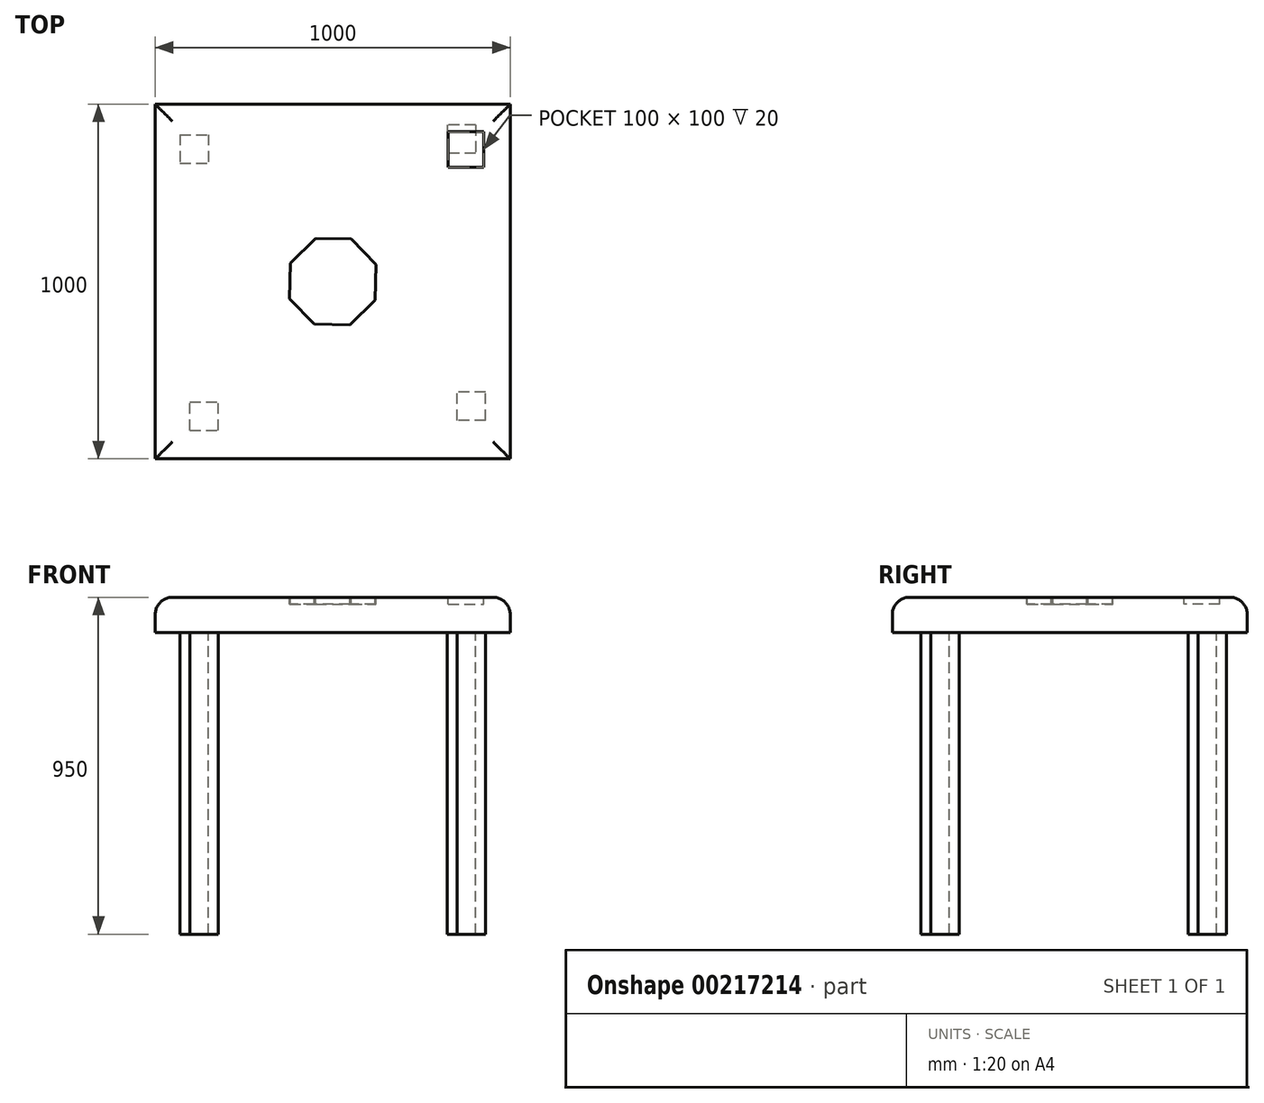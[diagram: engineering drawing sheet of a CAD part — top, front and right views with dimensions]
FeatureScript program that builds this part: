
annotation { "Feature Type Name" : "Feature", "Feature Type Description" : "" }
export const myFeature = defineFeature(function(context is Context, id is Id, definition is map)
    precondition{}
    {
        {
            var Q0;
            Q0=qCreatedBy(makeId("Top.planeOp"),FACE);
            var sketch = newSketch(context, id + "F0", { "sketchPlane" : qUnion([Q0])});
            skLineSegment(sketch, "E0.bottom", {"start": v(-500, 500) * mm, "end": v(500, 500) * mm});
            skLineSegment(sketch, "E0.top", {"start": v(-500, -500) * mm, "end": v(500, -500) * mm});
            skLineSegment(sketch, "E0.left", {"start": v(-500, 500) * mm, "end": v(-500, -500) * mm});
            skLineSegment(sketch, "E0.right", {"start": v(500, 500) * mm, "end": v(500, -500) * mm});
            skSolve(sketch);
        }
        {
            var Q0;
            Q0=makeQuery(id+"F0.imprint","IMPRINT",FACE,{"disambiguationData":[TD([[makeQuery(id+"F0.imprint","IMPRINT",EDGE,{"derivedFrom":sQuery(id+"F0.wireOp",EDGE,"E0.bottom")}),-1.0]])]});
            extrude(context, id + "F1", {"entities" : qUnion([Q0]), "depth" : 100 * mm});
        }
        {
            var Q0;
            Q0=makeQuery(id+"F1.opExtrude","CAP_FACE",FACE,{"disambiguationData":[OSD([sQuery(id+"F0.wireOp",EDGE,"E0.bottom"),sQuery(id+"F0.wireOp",EDGE,"E0.top"),sQuery(id+"F0.wireOp",EDGE,"E0.left"),sQuery(id+"F0.wireOp",EDGE,"E0.right")])],"isStart":false});
            fillet(context, id + "F2", {"entities" : qUnion([Q0]), "radius" : 48.28 * mm, "tangentPropagation" : true, "allowEdgeOverflow" : false});
        }
        {
            var Q0;
            Q0=makeQuery(id+"F1.opExtrude","CAP_FACE",FACE,{"disambiguationData":[OSD([sQuery(id+"F0.wireOp",EDGE,"E0.bottom"),sQuery(id+"F0.wireOp",EDGE,"E0.top"),sQuery(id+"F0.wireOp",EDGE,"E0.left"),sQuery(id+"F0.wireOp",EDGE,"E0.right")])],"isStart":false});
            var sketch = newSketch(context, id + "F3", { "sketchPlane" : qUnion([Q0])});
            skLineSegment(sketch, "E1.0", {"start": v(-119.83, 52.08) * mm, "end": v(-47.9, 121.56) * mm});
            skLineSegment(sketch, "E1.1", {"start": v(-47.9, 121.56) * mm, "end": v(52.08, 119.83) * mm});
            skLineSegment(sketch, "E1.2", {"start": v(52.08, 119.83) * mm, "end": v(121.56, 47.9) * mm});
            skLineSegment(sketch, "E1.3", {"start": v(121.56, 47.9) * mm, "end": v(119.83, -52.08) * mm});
            skLineSegment(sketch, "E1.4", {"start": v(119.83, -52.08) * mm, "end": v(47.9, -121.56) * mm});
            skLineSegment(sketch, "E1.5", {"start": v(47.9, -121.56) * mm, "end": v(-52.08, -119.83) * mm});
            skLineSegment(sketch, "E1.6", {"start": v(-52.08, -119.83) * mm, "end": v(-121.56, -47.9) * mm});
            skLineSegment(sketch, "E1.7", {"start": v(-121.56, -47.9) * mm, "end": v(-119.83, 52.08) * mm});
            skPoint(sketch, "E1.0.midPoint", {"position": v(-83.87, 86.82) * mm});
            skSolve(sketch);
        }
        {
            var Q0;
            Q0=makeQuery(id+"F3.imprint","IMPRINT",FACE,{"disambiguationData":[TD([[makeQuery(id+"F3.imprint","IMPRINT",EDGE,{"derivedFrom":sQuery(id+"F3.wireOp",EDGE,"E1.0")}),-1.0]])]});
            extrude(context, id + "F4", {"entities" : qUnion([Q0]), "operationType" : NewBodyOperationType.REMOVE, "oppositeDirection" : true, "depth" : 20 * mm});
        }
        {
            var Q0;
            Q0=makeQuery(id+"F1.opExtrude","CAP_FACE",FACE,{"disambiguationData":[OSD([sQuery(id+"F0.wireOp",EDGE,"E0.bottom"),sQuery(id+"F0.wireOp",EDGE,"E0.top"),sQuery(id+"F0.wireOp",EDGE,"E0.left"),sQuery(id+"F0.wireOp",EDGE,"E0.right")])],"isStart":false});
            var sketch = newSketch(context, id + "F5", { "sketchPlane" : qUnion([Q0])});
            skLineSegment(sketch, "E2.bottom", {"start": v(325.26, 422.02) * mm, "end": v(425.26, 422.02) * mm});
            skLineSegment(sketch, "E2.top", {"start": v(325.26, 322.02) * mm, "end": v(425.26, 322.02) * mm});
            skLineSegment(sketch, "E2.left", {"start": v(325.26, 422.02) * mm, "end": v(325.26, 322.02) * mm});
            skLineSegment(sketch, "E2.right", {"start": v(425.26, 422.02) * mm, "end": v(425.26, 322.02) * mm});
            skSolve(sketch);
        }
        {
            var Q0;
            Q0=makeQuery(id+"F5.imprint","IMPRINT",FACE,{"disambiguationData":[TD([[makeQuery(id+"F5.imprint","IMPRINT",EDGE,{"derivedFrom":sQuery(id+"F5.wireOp",EDGE,"E2.bottom")}),-1.0]])]});
            extrude(context, id + "F6", {"entities" : qUnion([Q0]), "operationType" : NewBodyOperationType.REMOVE, "oppositeDirection" : true, "depth" : 20 * mm});
        }
        {
            var Q0;
            Q0=makeQuery(id+"F1.opExtrude","CAP_FACE",FACE,{"disambiguationData":[OSD([sQuery(id+"F0.wireOp",EDGE,"E0.bottom"),sQuery(id+"F0.wireOp",EDGE,"E0.top"),sQuery(id+"F0.wireOp",EDGE,"E0.left"),sQuery(id+"F0.wireOp",EDGE,"E0.right")])],"isStart":true});
            var sketch = newSketch(context, id + "F7", { "sketchPlane" : qUnion([Q0])});
            skLineSegment(sketch, "E3.bottom", {"start": v(-402.4, 418.9) * mm, "end": v(-322.4, 418.9) * mm});
            skLineSegment(sketch, "E3.top", {"start": v(-402.4, 338.9) * mm, "end": v(-322.4, 338.9) * mm});
            skLineSegment(sketch, "E3.left", {"start": v(-402.4, 418.9) * mm, "end": v(-402.4, 338.9) * mm});
            skLineSegment(sketch, "E3.right", {"start": v(-322.4, 418.9) * mm, "end": v(-322.4, 338.9) * mm});
            skLineSegment(sketch, "E4.1.0", {"start": v(-350.32, -413.83) * mm, "end": v(-350.32, -333.83) * mm});
            skLineSegment(sketch, "E4.1.1", {"start": v(-430.32, -413.83) * mm, "end": v(-350.32, -413.83) * mm});
            skLineSegment(sketch, "E4.1.2", {"start": v(-430.32, -333.83) * mm, "end": v(-350.32, -333.83) * mm});
            skLineSegment(sketch, "E4.1.3", {"start": v(-430.32, -413.83) * mm, "end": v(-430.32, -333.83) * mm});
            skLineSegment(sketch, "E4.2.0", {"start": v(402.4, -361.75) * mm, "end": v(322.4, -361.75) * mm});
            skLineSegment(sketch, "E4.2.1", {"start": v(402.4, -441.75) * mm, "end": v(402.4, -361.75) * mm});
            skLineSegment(sketch, "E4.2.2", {"start": v(322.4, -441.75) * mm, "end": v(322.4, -361.75) * mm});
            skLineSegment(sketch, "E4.2.3", {"start": v(402.4, -441.75) * mm, "end": v(322.4, -441.75) * mm});
            skLineSegment(sketch, "E4.3.0", {"start": v(350.32, 390.97) * mm, "end": v(350.32, 310.97) * mm});
            skLineSegment(sketch, "E4.3.1", {"start": v(430.32, 390.97) * mm, "end": v(350.32, 390.97) * mm});
            skLineSegment(sketch, "E4.3.2", {"start": v(430.32, 310.97) * mm, "end": v(350.32, 310.97) * mm});
            skLineSegment(sketch, "E4.3.3", {"start": v(430.32, 390.97) * mm, "end": v(430.32, 310.97) * mm});
            skPoint(sketch, "E4.center", {"position": v(0, -11.43) * mm});
            skSolve(sketch);
        }
        {
            var Q0;
            Q0=makeQuery(id+"F7.imprint","IMPRINT",FACE,{"disambiguationData":[TD([[makeQuery(id+"F7.imprint","IMPRINT",EDGE,{"derivedFrom":sQuery(id+"F7.wireOp",EDGE,"E3.bottom")}),-1.0]])]});
            var Q1;
            Q1=makeQuery(id+"F7.imprint","IMPRINT",FACE,{"disambiguationData":[TD([[makeQuery(id+"F7.imprint","IMPRINT",EDGE,{"derivedFrom":sQuery(id+"F7.wireOp",EDGE,"E4.3.0")}),1.0]])]});
            var Q2;
            Q2=makeQuery(id+"F7.imprint","IMPRINT",FACE,{"disambiguationData":[TD([[makeQuery(id+"F7.imprint","IMPRINT",EDGE,{"derivedFrom":sQuery(id+"F7.wireOp",EDGE,"E4.2.0")}),1.0]])]});
            var Q3;
            Q3=makeQuery(id+"F7.imprint","IMPRINT",FACE,{"disambiguationData":[TD([[makeQuery(id+"F7.imprint","IMPRINT",EDGE,{"derivedFrom":sQuery(id+"F7.wireOp",EDGE,"E4.1.0")}),1.0]])]});
            extrude(context, id + "F8", {"entities" : qUnion([Q0, Q1, Q2, Q3]), "operationType" : NewBodyOperationType.ADD, "depth" : 850 * mm});
        }
    });
